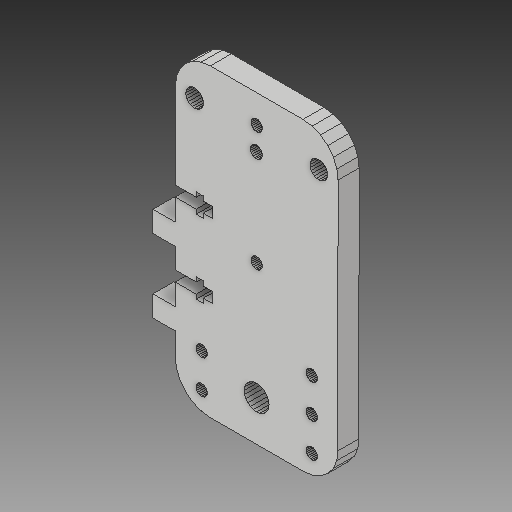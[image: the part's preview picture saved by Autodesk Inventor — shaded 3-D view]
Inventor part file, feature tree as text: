
AUTODESK INVENTOR PART (.ipt)
format: ipt  version: 2017 (Build 210142000, 142)  size: 583,168 bytes
history: native  units: mm
features: other x3, sketch x1
ambient origin geometry x8: Origin, YZ Plane, XZ Plane, XY Plane, X Axis, Y Axis, Z Axis, Center Point
bodies: Solid1 (feature_tree)
feature tree (4):
  other  "Hotend Rear Plate.ipt"
  other  "Solid1::Hotend Rear Plate.ipt"
  other  "TaggingFeature1"
  sketch  "Sketch1"  dims[d0=10.0mm]
